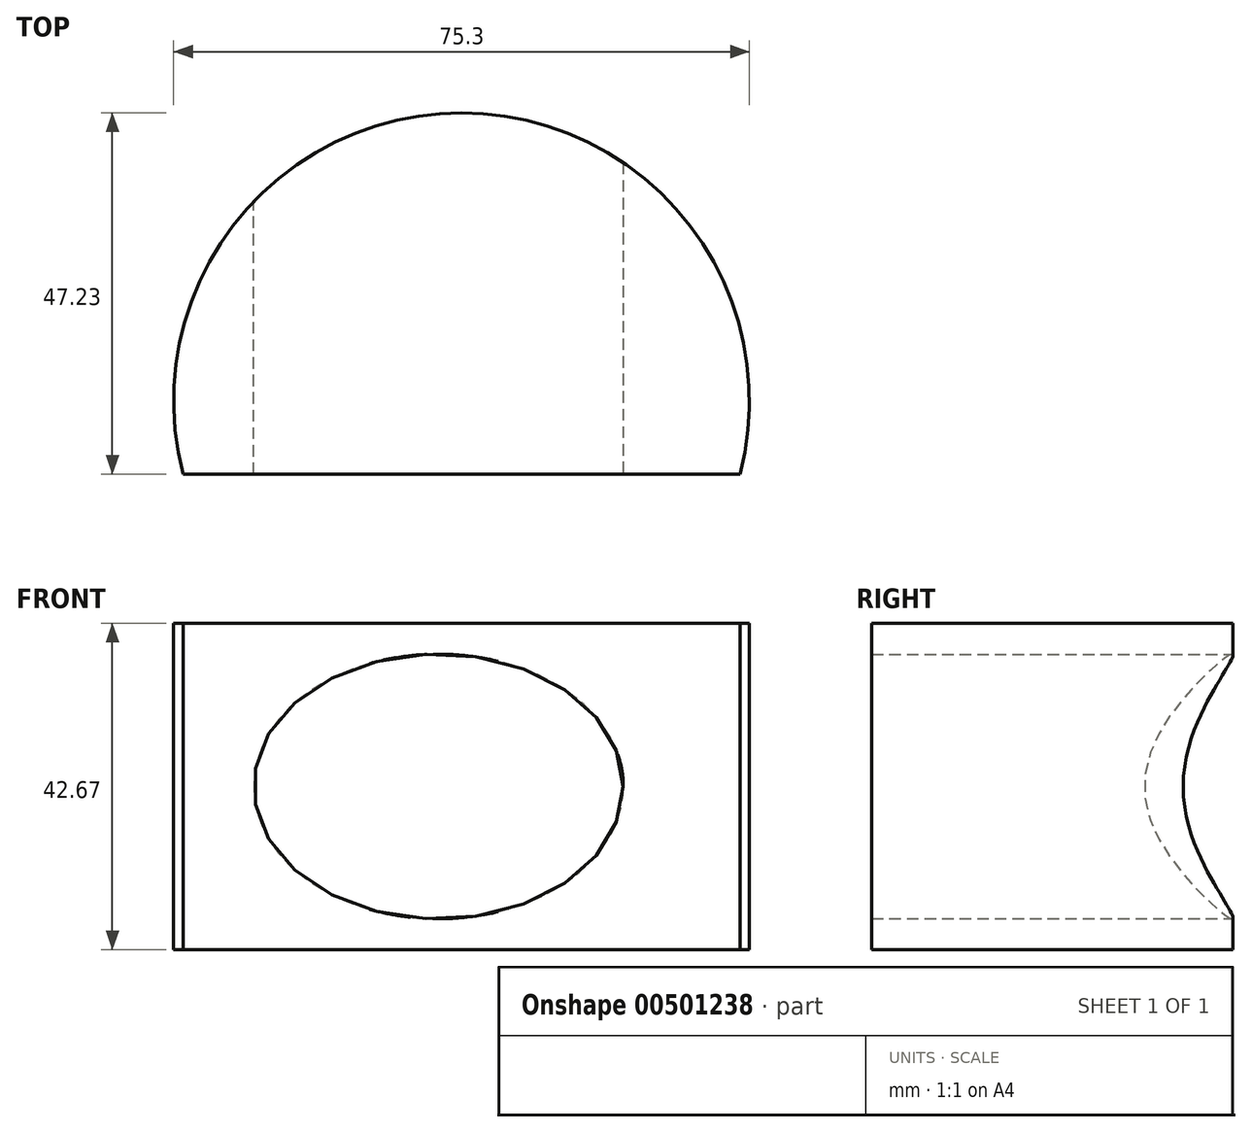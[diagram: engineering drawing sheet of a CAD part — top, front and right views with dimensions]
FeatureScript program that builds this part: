
annotation { "Feature Type Name" : "Feature", "Feature Type Description" : "" }
export const myFeature = defineFeature(function(context is Context, id is Id, definition is map)
    precondition{}
    {
        {
            var Q0;
            Q0=qCreatedBy(makeId("Top.planeOp"),FACE);
            var sketch = newSketch(context, id + "F0", { "sketchPlane" : qUnion([Q0])});
            skArc(sketch, "E0", {"start": v(72.81, 0) * mm, "mid": v(36.4, 47.23) * mm, "end": v(0, 0) * mm});
            skLineSegment(sketch, "E1", {"start": v(0, 0) * mm, "end": v(72.81, 0) * mm});
            skSolve(sketch);
        }
        {
            var Q0;
            Q0=makeQuery(id+"F0.imprint","IMPRINT",FACE,{"disambiguationData":[TD([[makeQuery(id+"F0.imprint","IMPRINT",EDGE,{"derivedFrom":sQuery(id+"F0.wireOp",EDGE,"E0")}),1.0]])]});
            extrude(context, id + "F1", {"entities" : qUnion([Q0]), "depth" : 42.67 * mm});
        }
        {
            var Q0;
            Q0=makeQuery(id+"F1.opExtrude","SWEPT_FACE",FACE,{"disambiguationData":[OSD([sQuery(id+"F0.wireOp",EDGE,"E1")])]});
            var sketch = newSketch(context, id + "F2", { "sketchPlane" : qUnion([Q0])});
            skEllipse(sketch, "E2", {"center": v(33.39, 21.34) * mm, "majorRadius": 24.18 * mm, "minorRadius": 17.3 * mm, "majorAxis": v(1, 0)});
            skPoint(sketch, "E2.centerSnap0", {"position": v(0, 21.34) * mm});
            skSolve(sketch);
        }
        {
            var Q0;
            Q0=makeQuery(id+"F2.imprint","IMPRINT",FACE,{"disambiguationData":[TD([[makeQuery(id+"F2.imprint","IMPRINT",EDGE,{"derivedFrom":sQuery(id+"F2.wireOp",EDGE,"E2")}),1.0]])]});
            extrude(context, id + "F3", {"entities" : qUnion([Q0]), "operationType" : NewBodyOperationType.REMOVE, "oppositeDirection" : true, "depth" : 58.93 * mm});
        }
    });
